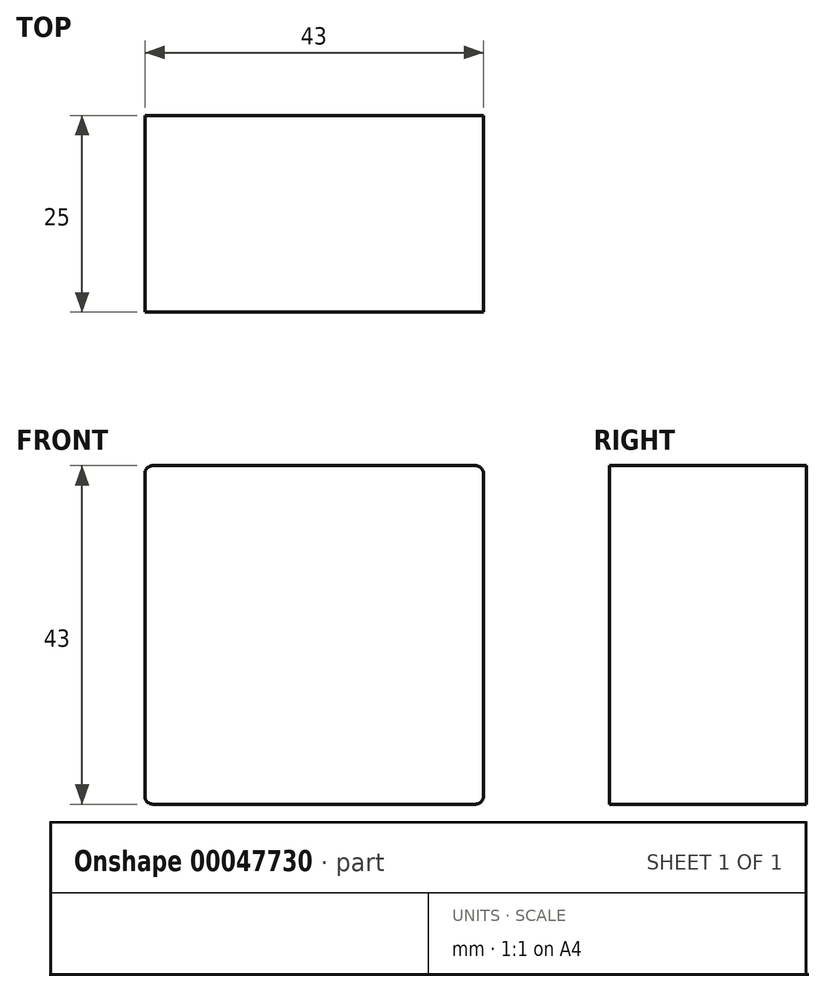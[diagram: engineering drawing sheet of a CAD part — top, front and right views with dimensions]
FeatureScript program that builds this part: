
annotation { "Feature Type Name" : "Feature", "Feature Type Description" : "" }
export const myFeature = defineFeature(function(context is Context, id is Id, definition is map)
    precondition{}
    {
        {
            var Q0;
            Q0=qCreatedBy(makeId("Front.planeOp"),FACE);
            var sketch = newSketch(context, id + "F0", { "sketchPlane" : qUnion([Q0])});
            skLineSegment(sketch, "E0.bottom", {"start": v(-19, 19) * mm, "end": v(19, 19) * mm, "construction": true});
            skLineSegment(sketch, "E0.top", {"start": v(-19, -19) * mm, "end": v(19, -19) * mm, "construction": true});
            skLineSegment(sketch, "E0.left", {"start": v(-19, 19) * mm, "end": v(-19, -19) * mm, "construction": true});
            skLineSegment(sketch, "E0.right", {"start": v(19, 19) * mm, "end": v(19, -19) * mm, "construction": true});
            skLineSegment(sketch, "E1", {"start": v(0, 19) * mm, "end": v(0, -19) * mm, "construction": true});
            skLineSegment(sketch, "E2.bottom", {"start": v(-20.5, 21.5) * mm, "end": v(20.5, 21.5) * mm});
            skLineSegment(sketch, "E2.top", {"start": v(-20.5, -21.5) * mm, "end": v(20.5, -21.5) * mm});
            skLineSegment(sketch, "E2.left", {"start": v(-21.5, 20.5) * mm, "end": v(-21.5, -20.5) * mm});
            skLineSegment(sketch, "E2.right", {"start": v(21.5, 20.5) * mm, "end": v(21.5, -20.5) * mm});
            skLineSegment(sketch, "E3", {"start": v(0, -19) * mm, "end": v(0, -21.5) * mm, "construction": true});
            skLineSegment(sketch, "E4", {"start": v(-19, 0) * mm, "end": v(-21.5, 0) * mm, "construction": true});
            skLineSegment(sketch, "E5.bottom", {"start": v(-16.5, 16.5) * mm, "end": v(16.5, 16.5) * mm, "construction": true});
            skLineSegment(sketch, "E5.top", {"start": v(-16.5, -16.5) * mm, "end": v(16.5, -16.5) * mm, "construction": true});
            skLineSegment(sketch, "E5.left", {"start": v(-16.5, 16.5) * mm, "end": v(-16.5, -16.5) * mm, "construction": true});
            skLineSegment(sketch, "E5.right", {"start": v(16.5, 16.5) * mm, "end": v(16.5, -16.5) * mm, "construction": true});
            skLineSegment(sketch, "E6.bottom", {"start": v(-13, 13) * mm, "end": v(13, 13) * mm, "construction": true});
            skLineSegment(sketch, "E6.top", {"start": v(-13, -13) * mm, "end": v(13, -13) * mm, "construction": true});
            skLineSegment(sketch, "E6.left", {"start": v(-13, 13) * mm, "end": v(-13, -13) * mm, "construction": true});
            skLineSegment(sketch, "E6.right", {"start": v(13, 13) * mm, "end": v(13, -13) * mm, "construction": true});
            skPoint(sketch, "E7", {"position": v(0, 16.5) * mm});
            skPoint(sketch, "E8", {"position": v(0, 13) * mm});
            skPoint(sketch, "E9.visualSharp", {"position": v(-21.5, 21.5) * mm});
            skArc(sketch, "E9.filletArc", {"start": v(-20.5, 21.5) * mm, "mid": v(-21.2, 21.2) * mm, "end": v(-21.5, 20.5) * mm});
            skPoint(sketch, "E10.visualSharp", {"position": v(21.5, 21.5) * mm});
            skArc(sketch, "E10.filletArc", {"start": v(21.5, 20.5) * mm, "mid": v(21.2, 21.2) * mm, "end": v(20.5, 21.5) * mm});
            skPoint(sketch, "E11.visualSharp", {"position": v(21.5, -21.5) * mm});
            skArc(sketch, "E11.filletArc", {"start": v(20.5, -21.5) * mm, "mid": v(21.2, -21.2) * mm, "end": v(21.5, -20.5) * mm});
            skPoint(sketch, "E12.visualSharp", {"position": v(-21.5, -21.5) * mm});
            skArc(sketch, "E12.filletArc", {"start": v(-21.5, -20.5) * mm, "mid": v(-21.2, -21.2) * mm, "end": v(-20.5, -21.5) * mm});
            skLineSegment(sketch, "E13", {"start": v(19, 0) * mm, "end": v(21.5, 0) * mm, "construction": true});
            skLineSegment(sketch, "E14", {"start": v(0, 19) * mm, "end": v(0, 21.5) * mm, "construction": true});
            skLineSegment(sketch, "E15", {"start": v(-16.5, 16.5) * mm, "end": v(-16.5, 19) * mm, "construction": true});
            skLineSegment(sketch, "E16", {"start": v(-16.5, -16.5) * mm, "end": v(-16.5, -19) * mm, "construction": true});
            skLineSegment(sketch, "E17", {"start": v(-16.5, 0) * mm, "end": v(-19, 0) * mm, "construction": true});
            skPoint(sketch, "E18", {"position": v(-13, 0) * mm});
            skPoint(sketch, "E19", {"position": v(0, 0) * mm});
            skCircle(sketch, "E20", {"center": v(-13, 13) * mm, "radius": 1.25 * mm, "construction": true});
            skCircle(sketch, "E21", {"center": v(13, 13) * mm, "radius": 1.25 * mm, "construction": true});
            skCircle(sketch, "E22", {"center": v(13, -13) * mm, "radius": 1.25 * mm, "construction": true});
            skCircle(sketch, "E23", {"center": v(-13, -13) * mm, "radius": 1.25 * mm, "construction": true});
            skCircle(sketch, "E24", {"center": v(-16.5, 16.5) * mm, "radius": 0.75 * mm, "construction": true});
            skCircle(sketch, "E25", {"center": v(16.5, 16.5) * mm, "radius": 0.75 * mm, "construction": true});
            skCircle(sketch, "E26", {"center": v(16.5, -16.5) * mm, "radius": 0.75 * mm, "construction": true});
            skCircle(sketch, "E27", {"center": v(-16.5, -16.5) * mm, "radius": 0.75 * mm, "construction": true});
            skSolve(sketch);
        }
        {
            var Q0;
            Q0 = qSketchRegion(id + "F0", true);
            extrude(context, id + "F1", {"entities" : qUnion([Q0]), "depth" : 25 * mm});
        }
    });
